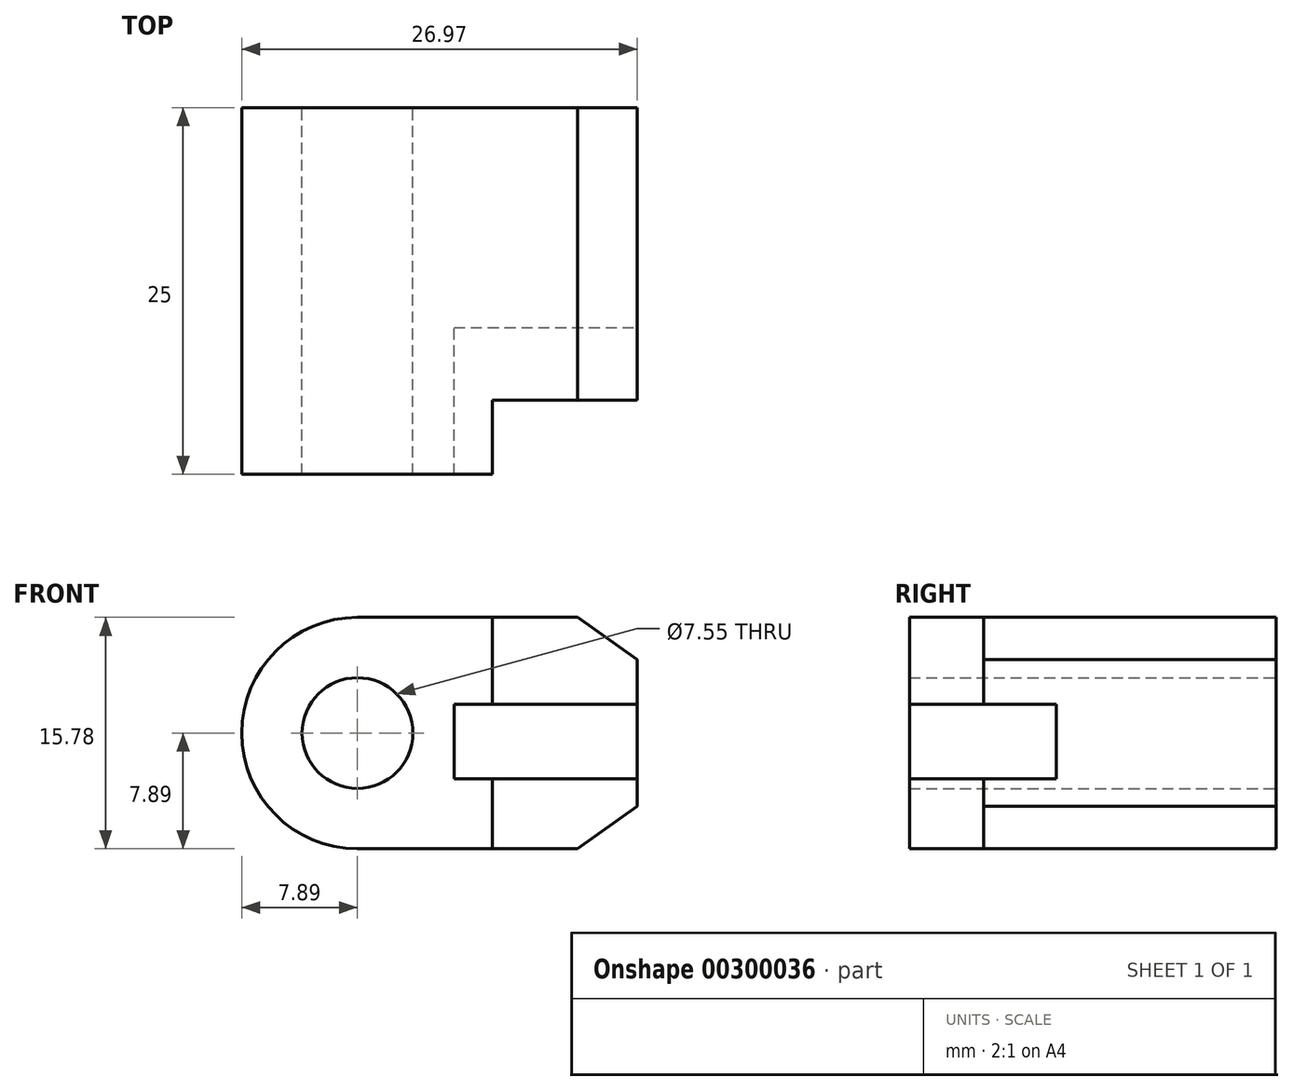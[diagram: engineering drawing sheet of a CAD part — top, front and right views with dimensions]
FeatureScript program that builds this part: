
annotation { "Feature Type Name" : "Feature", "Feature Type Description" : "" }
export const myFeature = defineFeature(function(context is Context, id is Id, definition is map)
    precondition{}
    {
        {
            var Q0;
            Q0=qCreatedBy(makeId("Front.planeOp"),FACE);
            var sketch = newSketch(context, id + "F0", { "sketchPlane" : qUnion([Q0])});
            skArc(sketch, "E0", {"start": v(7.48, 2.5) * mm, "mid": v(-7.89, 0) * mm, "end": v(7.48, -2.5) * mm});
            skLineSegment(sketch, "E1", {"start": v(-7.64, 1.94) * mm, "end": v(-3.24, 1.94) * mm});
            skLineSegment(sketch, "E2", {"start": v(-7.48, -2.5) * mm, "end": v(-2.88, -2.5) * mm});
            skLineSegment(sketch, "E3", {"start": v(2.83, 2.5) * mm, "end": v(7.48, 2.5) * mm});
            skLineSegment(sketch, "E4", {"start": v(2.83, -2.5) * mm, "end": v(7.48, -2.5) * mm});
            skLineSegment(sketch, "E5", {"start": v(7.48, 2.5) * mm, "end": v(19.08, 2.5) * mm});
            skLineSegment(sketch, "E6", {"start": v(7.48, -2.5) * mm, "end": v(19.08, -2.5) * mm});
            skLineSegment(sketch, "E7", {"start": v(19.08, 2.5) * mm, "end": v(19.08, 5) * mm});
            skLineSegment(sketch, "E8", {"start": v(19.08, 5) * mm, "end": v(15, 7.89) * mm});
            skLineSegment(sketch, "E9", {"start": v(15, 7.89) * mm, "end": v(0, 7.89) * mm});
            skLineSegment(sketch, "E10", {"start": v(19.08, -2.5) * mm, "end": v(19.08, -5) * mm});
            skLineSegment(sketch, "E11", {"start": v(19.08, -5) * mm, "end": v(15, -7.89) * mm});
            skLineSegment(sketch, "E12", {"start": v(15, -7.89) * mm, "end": v(0, -7.89) * mm});
            skCircle(sketch, "E13", {"center": v(0, 0) * mm, "radius": 3.78 * mm});
            skLineSegment(sketch, "E14", {"start": v(19.08, 2.5) * mm, "end": v(19.08, -2.5) * mm});
            skSolve(sketch);
        }
        {
            var Q0;
            Q0 = qSketchRegion(id + "F0", true);
            extrude(context, id + "F1", {"entities" : qUnion([Q0]), "depth" : 25 * mm});
        }
        {
            var Q0;
            Q0=makeQuery(id+"F1.opExtrude","SWEPT_FACE",FACE,{"disambiguationData":[OSD([sQuery(id+"F0.wireOp",EDGE,"E9")])]});
            var sketch = newSketch(context, id + "F2", { "sketchPlane" : qUnion([Q0])});
            skLineSegment(sketch, "E15.bottom", {"start": v(9.19, -25) * mm, "end": v(19.13, -25) * mm});
            skLineSegment(sketch, "E15.top", {"start": v(9.19, -19.95) * mm, "end": v(19.13, -19.95) * mm});
            skLineSegment(sketch, "E15.left", {"start": v(9.19, -25) * mm, "end": v(9.19, -19.95) * mm});
            skLineSegment(sketch, "E15.right", {"start": v(19.13, -25) * mm, "end": v(19.13, -19.95) * mm});
            skSolve(sketch);
        }
        {
            var Q0;
            Q0 = qSketchRegion(id + "F2", true);
            extrude(context, id + "F3", {"entities" : qUnion([Q0]), "operationType" : NewBodyOperationType.REMOVE, "endBound" : BoundingType.THROUGH_ALL, "oppositeDirection" : true, "depth" : 25 * mm});
        }
        {
            var Q0;
            Q0=makeQuery(id+"F1.opExtrude","SWEPT_FACE",FACE,{"disambiguationData":[OSD([sQuery(id+"F0.wireOp",EDGE,"E7"),sQuery(id+"F0.wireOp",EDGE,"E10"),sQuery(id+"F0.wireOp",EDGE,"E14")])]});
            var sketch = newSketch(context, id + "F4", { "sketchPlane" : qUnion([Q0])});
            skLineSegment(sketch, "E16.bottom", {"start": v(-25.18, 1.97) * mm, "end": v(-15, 1.97) * mm});
            skLineSegment(sketch, "E16.top", {"start": v(-25.18, -3.13) * mm, "end": v(-15, -3.13) * mm});
            skLineSegment(sketch, "E16.left", {"start": v(-25.18, 1.97) * mm, "end": v(-25.18, -3.13) * mm});
            skLineSegment(sketch, "E16.right", {"start": v(-15, 1.97) * mm, "end": v(-15, -3.13) * mm});
            skSolve(sketch);
        }
        {
            var Q0;
            Q0 = qSketchRegion(id + "F4", true);
            extrude(context, id + "F5", {"entities" : qUnion([Q0]), "operationType" : NewBodyOperationType.REMOVE, "endBound" : BoundingType.SYMMETRIC, "oppositeDirection" : true, "depth" : 25 * mm});
        }
    });
